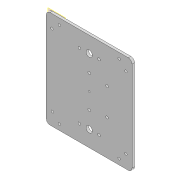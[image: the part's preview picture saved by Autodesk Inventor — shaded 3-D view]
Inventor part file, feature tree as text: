
AUTODESK INVENTOR PART (.ipt)
format: ipt  version: 2020 (Build 240168000, 168)  size: 185,856 bytes
history: native  units: mm
features: other x23, extrude x5, sketch x5
ambient origin geometry x8: Origin, YZ Plane, XZ Plane, XY Plane, X Axis, Y Axis, Z Axis, Center Point
bodies: Body1 (feature_tree)
feature tree (33):
  other  "Sólido1"
  other  "Plano de trabalho1"
  extrude  "Extrusão1"  Depth=4.0mm
  extrude  "Extrusão2"  Depth=3.0mm
  extrude  "Extrusão3"  Depth=4.0mm
  extrude  "Extrusão4"  Depth=4.2mm
  extrude  "Extrusão5"  Depth=10.0mm
  sketch  "Esboço1"  dims[d0=4.0mm d1=0.0mm d2=10.1mm]
  other  "Referência1"
  other  "Referência2"
  other  "Referência3"
  other  "Referência4"
  sketch  "Esboço2"  dims[d3=4.2mm d4=3.0mm]
  other  "Referência5"
  other  "Referência6"
  other  "Referência7"
  other  "Referência8"
  other  "Referência9"
  sketch  "Esboço3"  dims[d5=4.0mm d6=0.0mm d7=32.0mm]
  sketch  "Esboço4"  dims[d8=32.0mm d9=4.2mm]
  sketch  "Esboço5"  dims[d10=4.2mm d11=4.2mm d12=4.2mm d13=4.0mm d14=0.0mm d15=4.2mm d16=4.2mm d17=4.0mm d18=0.0mm d19=10.0mm d20=10.1mm d21=10.1mm d22=10.0mm d23=0.0mm]
  other  "<userpath>\OneDrive\Área de Trabalho\Calorimetro 2022\Inventor\Calorímetro.iam"
  other  "Calorímetro.iam"
  other  "suporte_fechamento:1"
  other  "suporte_fechamento:2"
  other  "suporte_fechamento2:2"
  other  "suporte_fechamento2:3"
  other  "parte_superior:1"
  other  "guia_10mm:1"
  other  "guia_10mm:2"
  other  "Montagem_corpo_menor:1"
  other  "corpo_1_menor:4"
  other  "Inferior_encaixe:1"
